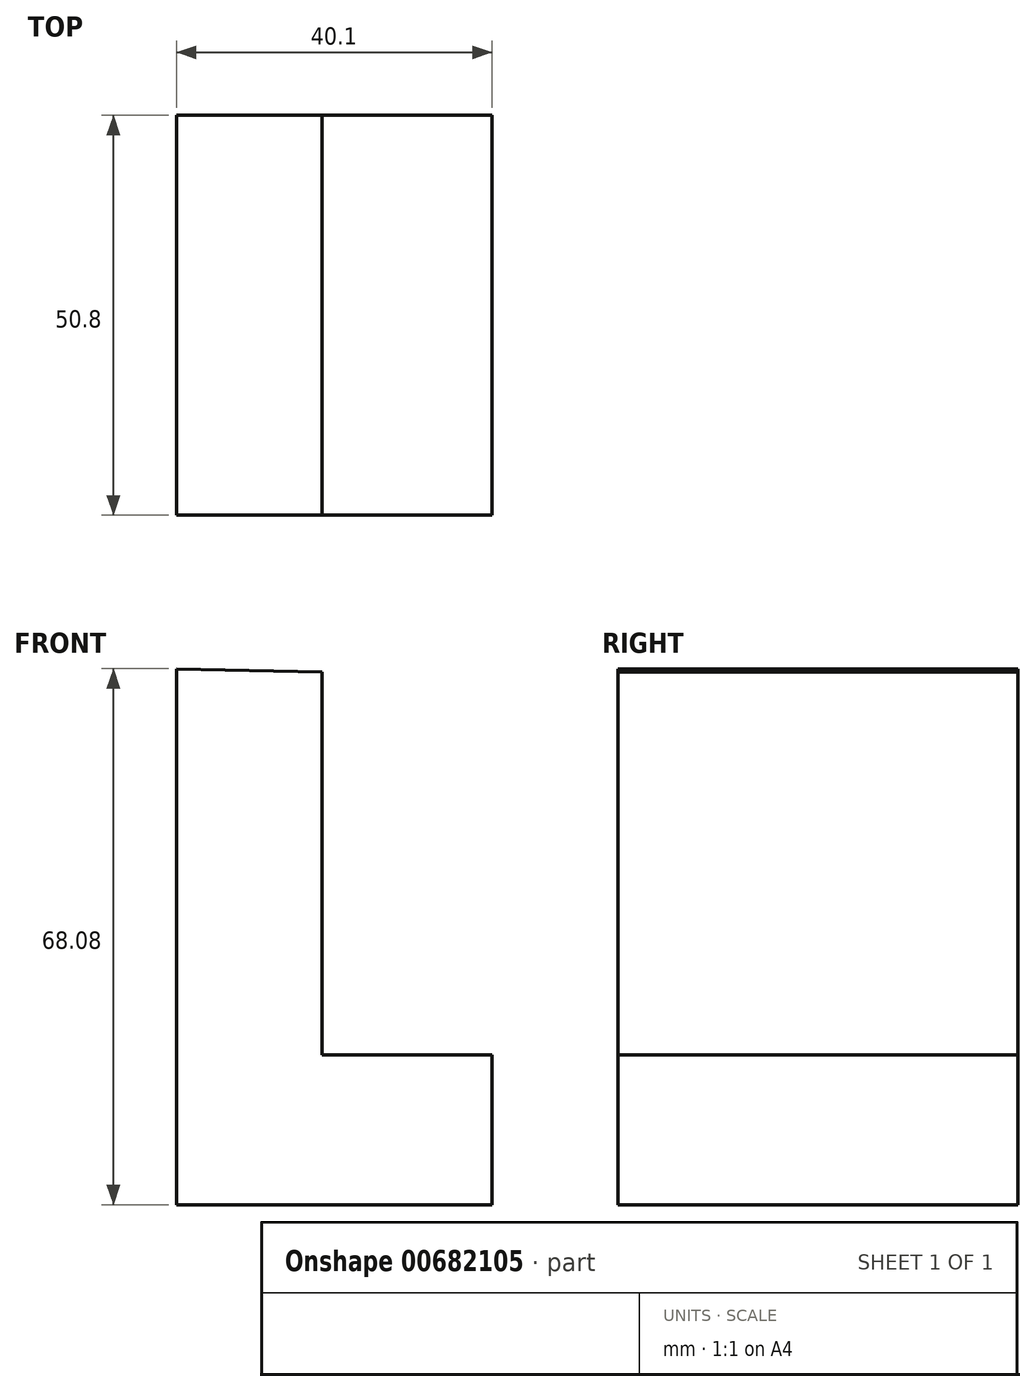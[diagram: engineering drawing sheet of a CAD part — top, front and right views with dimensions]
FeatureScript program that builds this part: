
annotation { "Feature Type Name" : "Feature", "Feature Type Description" : "" }
export const myFeature = defineFeature(function(context is Context, id is Id, definition is map)
    precondition{}
    {
        {
            var Q0;
            Q0=qCreatedBy(makeId("Front.planeOp"),FACE);
            var sketch = newSketch(context, id + "F0", { "sketchPlane" : qUnion([Q0])});
            skLineSegment(sketch, "E0", {"start": v(-53.18, 68.08) * mm, "end": v(-53.18, 0) * mm});
            skLineSegment(sketch, "E1", {"start": v(-53.18, 0) * mm, "end": v(-13.08, 0) * mm});
            skLineSegment(sketch, "E2", {"start": v(-13.08, 0) * mm, "end": v(-13.08, 19) * mm});
            skLineSegment(sketch, "E3", {"start": v(-13.08, 19) * mm, "end": v(-34.66, 19) * mm});
            skLineSegment(sketch, "E4", {"start": v(-34.66, 19) * mm, "end": v(-34.66, 67.7) * mm});
            skLineSegment(sketch, "E5", {"start": v(-34.66, 67.7) * mm, "end": v(-53.18, 68.08) * mm});
            skSolve(sketch);
        }
        {
            var Q0;
            Q0 = qSketchRegion(id + "F0", true);
            extrude(context, id + "F1", {"entities" : qUnion([Q0]), "depth" : 50.8 * mm, "offsetDistance" : 25.4 * mm});
        }
    });
